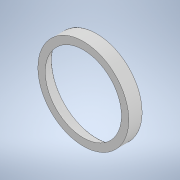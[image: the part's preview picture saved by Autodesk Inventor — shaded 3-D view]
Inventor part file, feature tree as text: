
AUTODESK INVENTOR PART (.ipt)
format: ipt  version: 2021 (Build 250183000, 183)  size: 109,056 bytes
history: native  units: mm
features: revolve x1, sketch x1
ambient origin geometry x8: Origin, YZ Plane, XZ Plane, XY Plane, X Axis, Y Axis, Z Axis, Center Point
bodies: Solid1 (feature_tree)
feature tree (2):
  revolve  "Revolution1"  [1 undecoded]
  sketch  "Sketch1"  dims[d0=4.886922mm d2=71.65mm d3=90.0deg d4=0.4mm d5=21.0mm]
note: 1 required parameter value undecoded (feature->parameter linkage not recoverable at this tier; creation-order binding heuristic only, values carry confidence <= 0.55)
